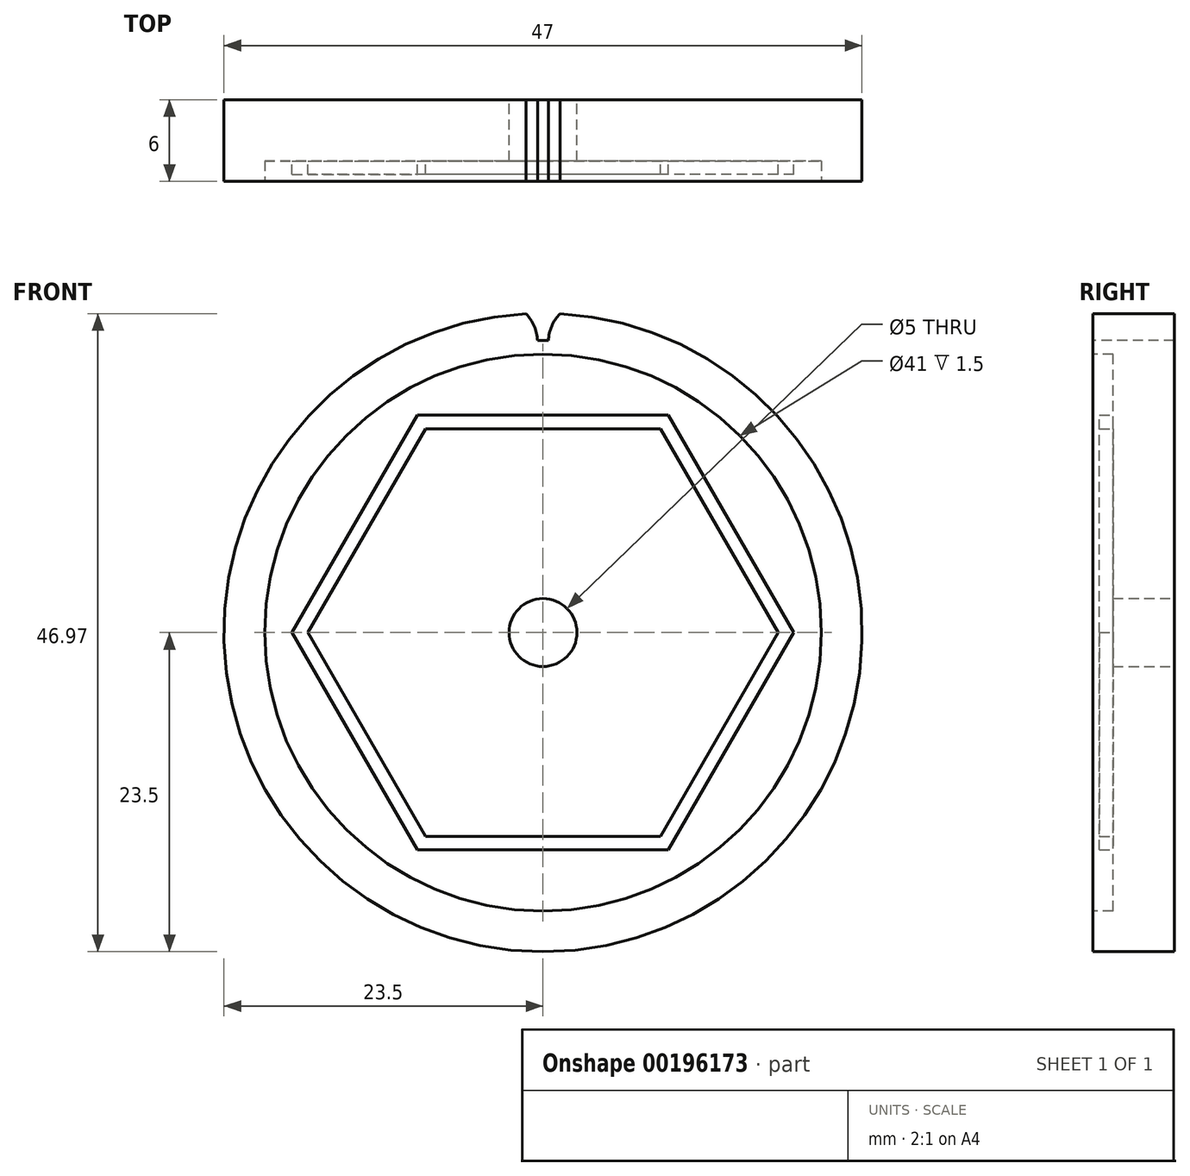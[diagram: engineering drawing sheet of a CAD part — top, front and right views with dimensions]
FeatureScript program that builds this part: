
annotation { "Feature Type Name" : "Feature", "Feature Type Description" : "" }
export const myFeature = defineFeature(function(context is Context, id is Id, definition is map)
    precondition{}
    {
        {
            var Q0;
            Q0=qCreatedBy(makeId("Front.planeOp"),FACE);
            var sketch = newSketch(context, id + "F0", { "sketchPlane" : qUnion([Q0])});
            skCircle(sketch, "E0", {"center": v(0, 0) * mm, "radius": 23.5 * mm});
            skCircle(sketch, "E1", {"center": v(0, 0) * mm, "radius": 2.5 * mm});
            skSolve(sketch);
        }
        {
            var Q0;
            Q0 = qSketchRegion(id + "F0", true);
            extrude(context, id + "F1", {"entities" : qUnion([Q0]), "depth" : 3 * mm, "hasSecondDirection" : true, "secondDirectionOppositeDirection" : true, "secondDirectionDepth" : 3 * mm});
        }
        {
            var Q0;
            Q0=qCreatedBy(makeId("Top.planeOp"),FACE);
            var sketch = newSketch(context, id + "F2", { "sketchPlane" : qUnion([Q0])});
            skLineSegment(sketch, "E2", {"start": v(0, 0) * mm, "end": v(0, 10.53) * mm, "construction": true});
            skSolve(sketch);
        }
        {
            var Q0;
            Q0=makeQuery(id+"F1.opExtrude","CAP_FACE",FACE,{"disambiguationData":[OSD([sQuery(id+"F0.wireOp",EDGE,"E0")])],"isStart":false});
            var sketch = newSketch(context, id + "F3", { "sketchPlane" : qUnion([Q0])});
            skCircle(sketch, "E3", {"center": v(0, 0) * mm, "radius": 20.5 * mm});
            skSolve(sketch);
        }
        {
            var Q0;
            Q0 = qSketchRegion(id + "F3", true);
            extrude(context, id + "F4", {"entities" : qUnion([Q0]), "operationType" : NewBodyOperationType.REMOVE, "oppositeDirection" : true, "depth" : 1.5 * mm});
        }
        {
            var Q0;
            Q0=makeQuery(id+"F4.boolean.opBoolean","COPY",FACE,{"derivedFrom":makeQuery(id+"F4.opExtrude","CAP_FACE",FACE,{"disambiguationData":[OSD([sQuery(id+"F3.wireOp",EDGE,"E3")])],"isStart":false})});
            var sketch = newSketch(context, id + "F5", { "sketchPlane" : qUnion([Q0])});
            skLineSegment(sketch, "E4", {"start": v(0, 0) * mm, "end": v(0, 16) * mm, "construction": true});
            skLineSegment(sketch, "E5", {"start": v(0, 0) * mm, "end": v(-18.48, 0) * mm, "construction": true});
            skCircle(sketch, "E6.cCircle", {"center": v(0, 0) * mm, "radius": 16 * mm, "construction": true});
            skLineSegment(sketch, "E6.0", {"start": v(-18.48, 0) * mm, "end": v(-9.24, 16) * mm});
            skLineSegment(sketch, "E6.1", {"start": v(-9.24, 16) * mm, "end": v(9.24, 16) * mm});
            skLineSegment(sketch, "E6.2", {"start": v(9.24, 16) * mm, "end": v(18.48, 0) * mm});
            skLineSegment(sketch, "E6.3", {"start": v(18.48, 0) * mm, "end": v(9.24, -16) * mm});
            skLineSegment(sketch, "E6.4", {"start": v(9.24, -16) * mm, "end": v(-9.24, -16) * mm});
            skLineSegment(sketch, "E6.5", {"start": v(-9.24, -16) * mm, "end": v(-18.48, 0) * mm});
            skPoint(sketch, "E6.0.midPoint", {"position": v(-13.86, 8) * mm});
            skLineSegment(sketch, "E7.0", {"start": v(17.32, 0) * mm, "end": v(8.66, -15) * mm});
            skLineSegment(sketch, "E7.1", {"start": v(-8.66, -15) * mm, "end": v(-17.32, 0) * mm});
            skLineSegment(sketch, "E7.2", {"start": v(-17.32, 0) * mm, "end": v(-8.66, 15) * mm});
            skLineSegment(sketch, "E7.3", {"start": v(8.66, -15) * mm, "end": v(-8.66, -15) * mm});
            skLineSegment(sketch, "E7.4", {"start": v(-8.66, 15) * mm, "end": v(8.66, 15) * mm});
            skLineSegment(sketch, "E7.5", {"start": v(8.66, 15) * mm, "end": v(17.32, 0) * mm});
            skSolve(sketch);
        }
        {
            var Q0;
            Q0 = qSketchRegion(id + "F5", true);
            extrude(context, id + "F6", {"entities" : qUnion([Q0]), "operationType" : NewBodyOperationType.ADD, "depth" : 1 * mm});
        }
        {
            var Q0;
            Q0=qCreatedBy(makeId("Front.planeOp"),FACE);
            var sketch = newSketch(context, id + "F7", { "sketchPlane" : qUnion([Q0])});
            skLineSegment(sketch, "E8", {"start": v(0, 0) * mm, "end": v(0, 23.5) * mm, "construction": true});
            skArc(sketch, "E9", {"start": v(0.4, 21.5) * mm, "mid": v(0.2, 21.5) * mm, "end": v(0, 21.5) * mm});
            skLineSegment(sketch, "E10", {"start": v(0, 0) * mm, "end": v(1.25, 23.47) * mm, "construction": true});
            skArc(sketch, "E11", {"start": v(1.25, 23.47) * mm, "mid": v(0.64, 22.56) * mm, "end": v(0.4, 21.5) * mm});
            skArc(sketch, "E12.0", {"start": v(1.25, 23.47) * mm, "mid": v(0, 23.5) * mm, "end": v(-1.25, 23.47) * mm});
            skLineSegment(sketch, "E13.MirrorCS", {"start": v(0, 0) * mm, "end": v(-1.25, 23.47) * mm, "construction": true});
            skArc(sketch, "E14.MirrorCS", {"start": v(-1.25, 23.47) * mm, "mid": v(-0.64, 22.56) * mm, "end": v(-0.4, 21.5) * mm});
            skArc(sketch, "E15.MirrorCS", {"start": v(-0.4, 21.5) * mm, "mid": v(-0.2, 21.5) * mm, "end": v(0, 21.5) * mm});
            skPoint(sketch, "E16.orphan", {"position": v(1.14, 21.47) * mm});
            skPoint(sketch, "E17.orphan", {"position": v(-1.14, 21.47) * mm});
            skSolve(sketch);
        }
        {
            var Q0;
            Q0 = qSketchRegion(id + "F7", true);
            extrude(context, id + "F8", {"entities" : qUnion([Q0]), "operationType" : NewBodyOperationType.REMOVE, "endBound" : BoundingType.THROUGH_ALL, "oppositeDirection" : true, "depth" : 25 * mm, "hasSecondDirection" : true, "secondDirectionBound" : SecondDirectionBoundingType.THROUGH_ALL, "secondDirectionOppositeDirection" : false, "secondDirectionDepth" : 25 * mm});
        }
    });
